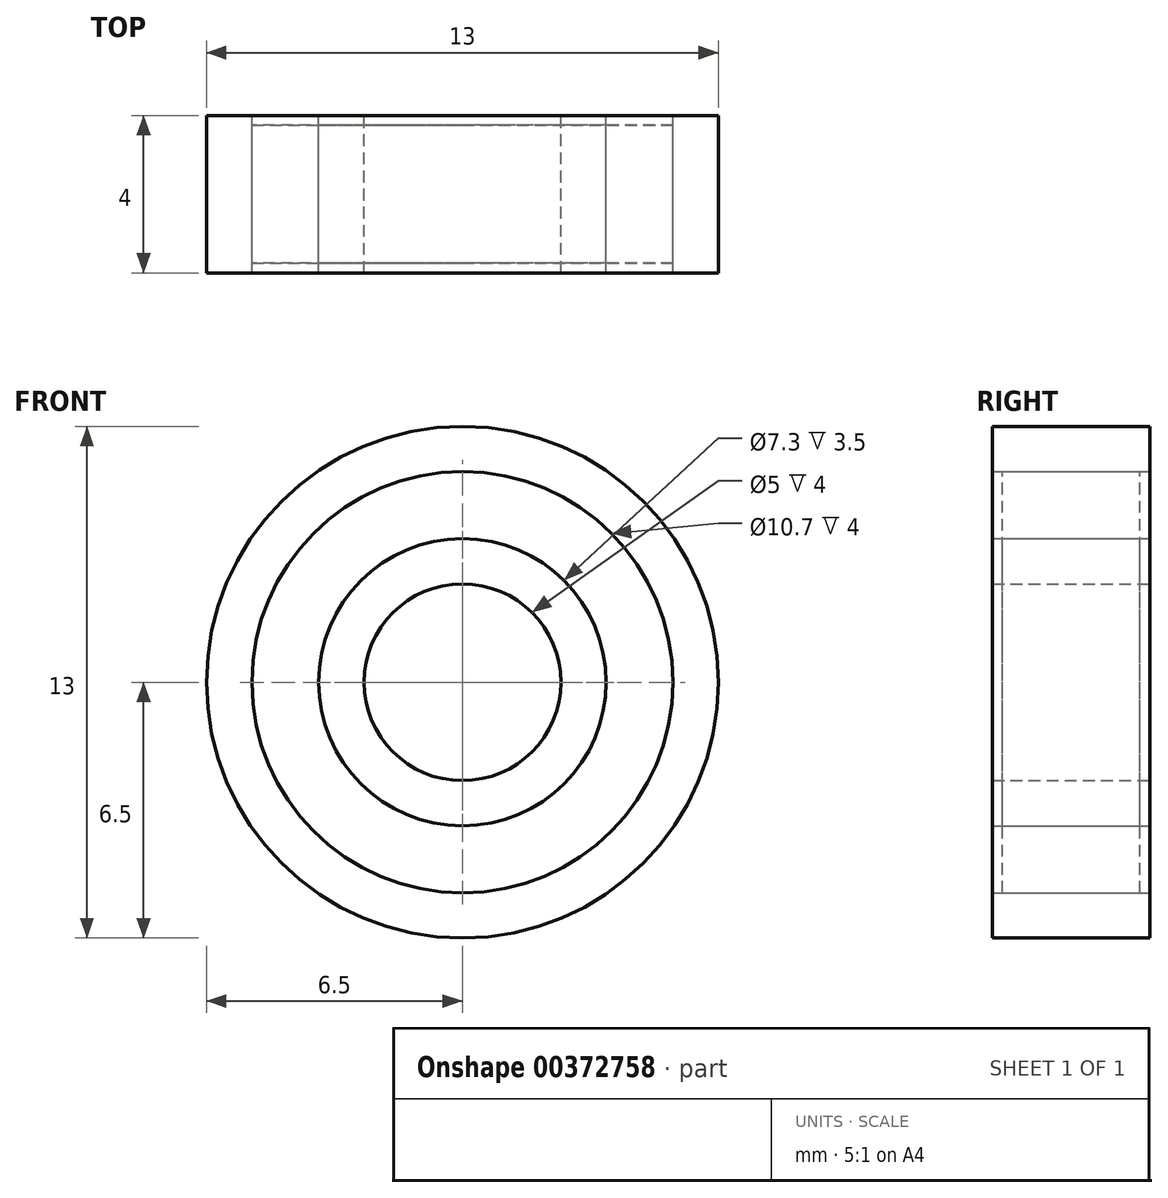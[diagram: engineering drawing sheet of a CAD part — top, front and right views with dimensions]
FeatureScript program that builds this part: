
annotation { "Feature Type Name" : "Feature", "Feature Type Description" : "" }
export const myFeature = defineFeature(function(context is Context, id is Id, definition is map)
    precondition{}
    {
        {
            assignVariable(context, id + "F0", {"name" : "e", "anyValue" : 4});
        }
        {
            var Q0;
            Q0=qCreatedBy(makeId("Front.planeOp"),FACE);
            var sketch = newSketch(context, id + "F1", { "sketchPlane" : qUnion([Q0])});
            skCircle(sketch, "E0", {"center": v(0, 0) * mm, "radius": 6.5 * mm});
            skCircle(sketch, "E1", {"center": v(0, 0) * mm, "radius": 5.35 * mm});
            skSolve(sketch);
        }
        {
            var Q0;
            Q0=qSketchRegion(id+"F1",true);
            extrude(context, id + "F2", {"entities" : qUnion([Q0]), "depth" : (getVariable(context, 'e')) * mm, "symmetric" : true});
        }
        {
            var Q0;
            Q0=qCreatedBy(makeId("Front.planeOp"),FACE);
            var sketch = newSketch(context, id + "F3", { "sketchPlane" : qUnion([Q0])});
            skCircle(sketch, "E2", {"center": v(0, 0) * mm, "radius": 2.5 * mm});
            skCircle(sketch, "E3", {"center": v(0, 0) * mm, "radius": 3.65 * mm});
            skSolve(sketch);
        }
        {
            var Q0;
            Q0=qSketchRegion(id+"F3",true);
            extrude(context, id + "F4", {"entities" : qUnion([Q0]), "depth" : (getVariable(context, 'e')) * mm, "symmetric" : true});
        }
        {
            var Q0;
            Q0=qCreatedBy(makeId("Front.planeOp"),FACE);
            var sketch = newSketch(context, id + "F5", { "sketchPlane" : qUnion([Q0])});
            skCircle(sketch, "E4", {"center": v(0, 0) * mm, "radius": 3.65 * mm});
            skCircle(sketch, "E5", {"center": v(0, 0) * mm, "radius": 5.35 * mm});
            skSolve(sketch);
        }
        {
            var Q0;
            Q0=qSketchRegion(id+"F5",true);
            extrude(context, id + "F6", {"entities" : qUnion([Q0]), "depth" : (getVariable(context, 'e') - 0.5) * mm, "symmetric" : true});
        }
    });
